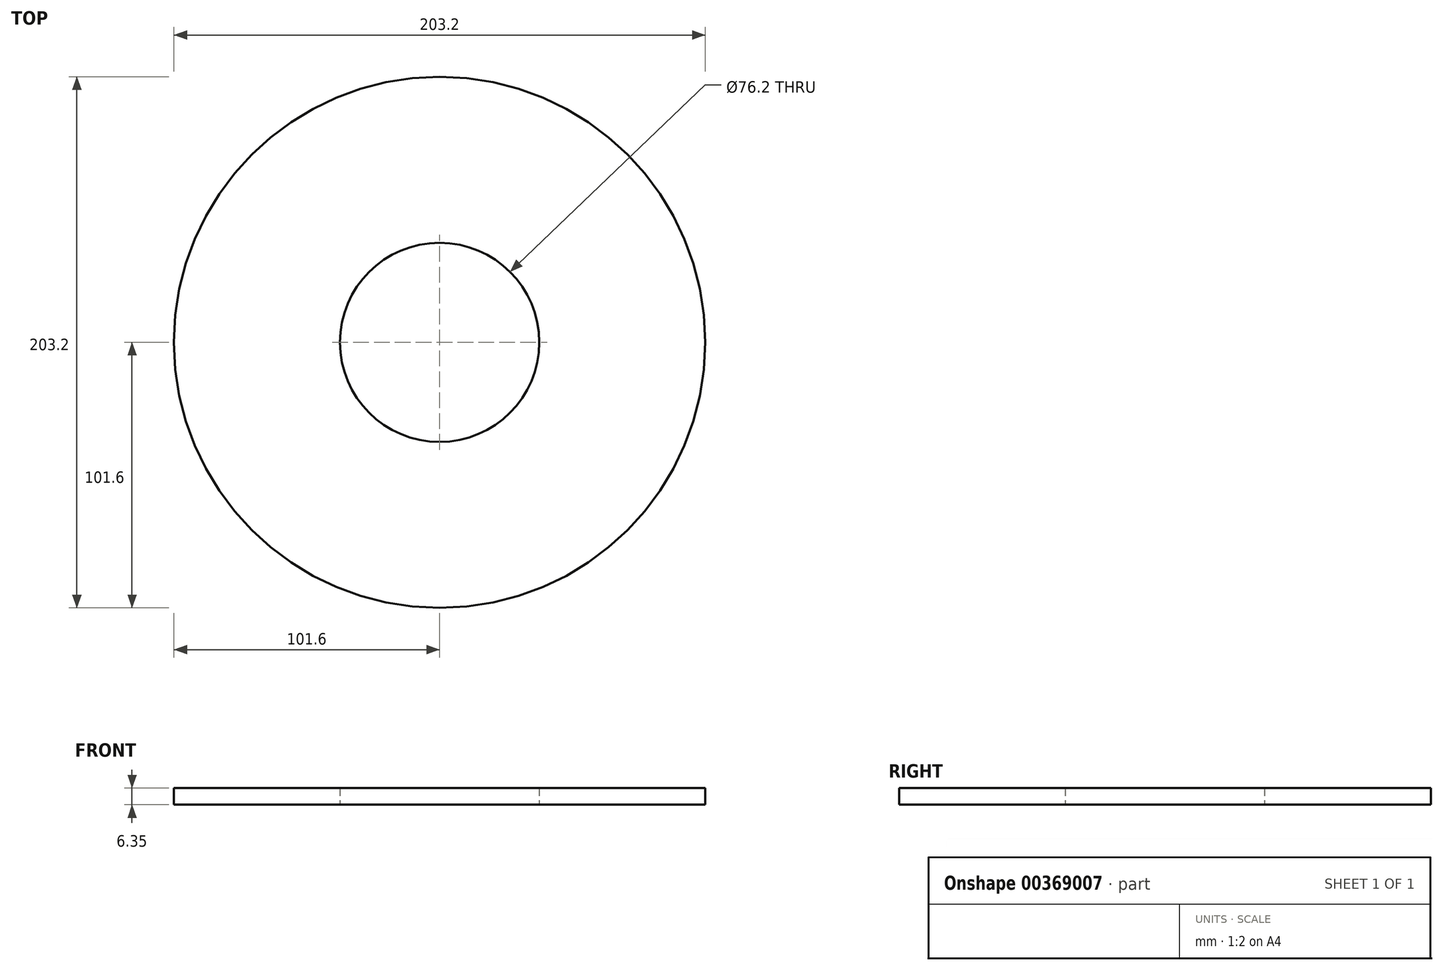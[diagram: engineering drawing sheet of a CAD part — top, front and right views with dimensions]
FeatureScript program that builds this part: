
annotation { "Feature Type Name" : "Feature", "Feature Type Description" : "" }
export const myFeature = defineFeature(function(context is Context, id is Id, definition is map)
    precondition{}
    {
        {
            var Q0;
            Q0=qCreatedBy(makeId("Top.planeOp"),FACE);
            var sketch = newSketch(context, id + "F0", { "sketchPlane" : qUnion([Q0])});
            skCircle(sketch, "E0", {"center": v(0, 0) * mm, "radius": 38.1 * mm});
            skCircle(sketch, "E1", {"center": v(0, 0) * mm, "radius": 101.6 * mm});
            skSolve(sketch);
        }
        {
            var Q0;
            Q0 = qSketchRegion(id + "F0", true);
            extrude(context, id + "F1", {"entities" : qUnion([Q0]), "depth" : 6.35 * mm});
        }
    });
